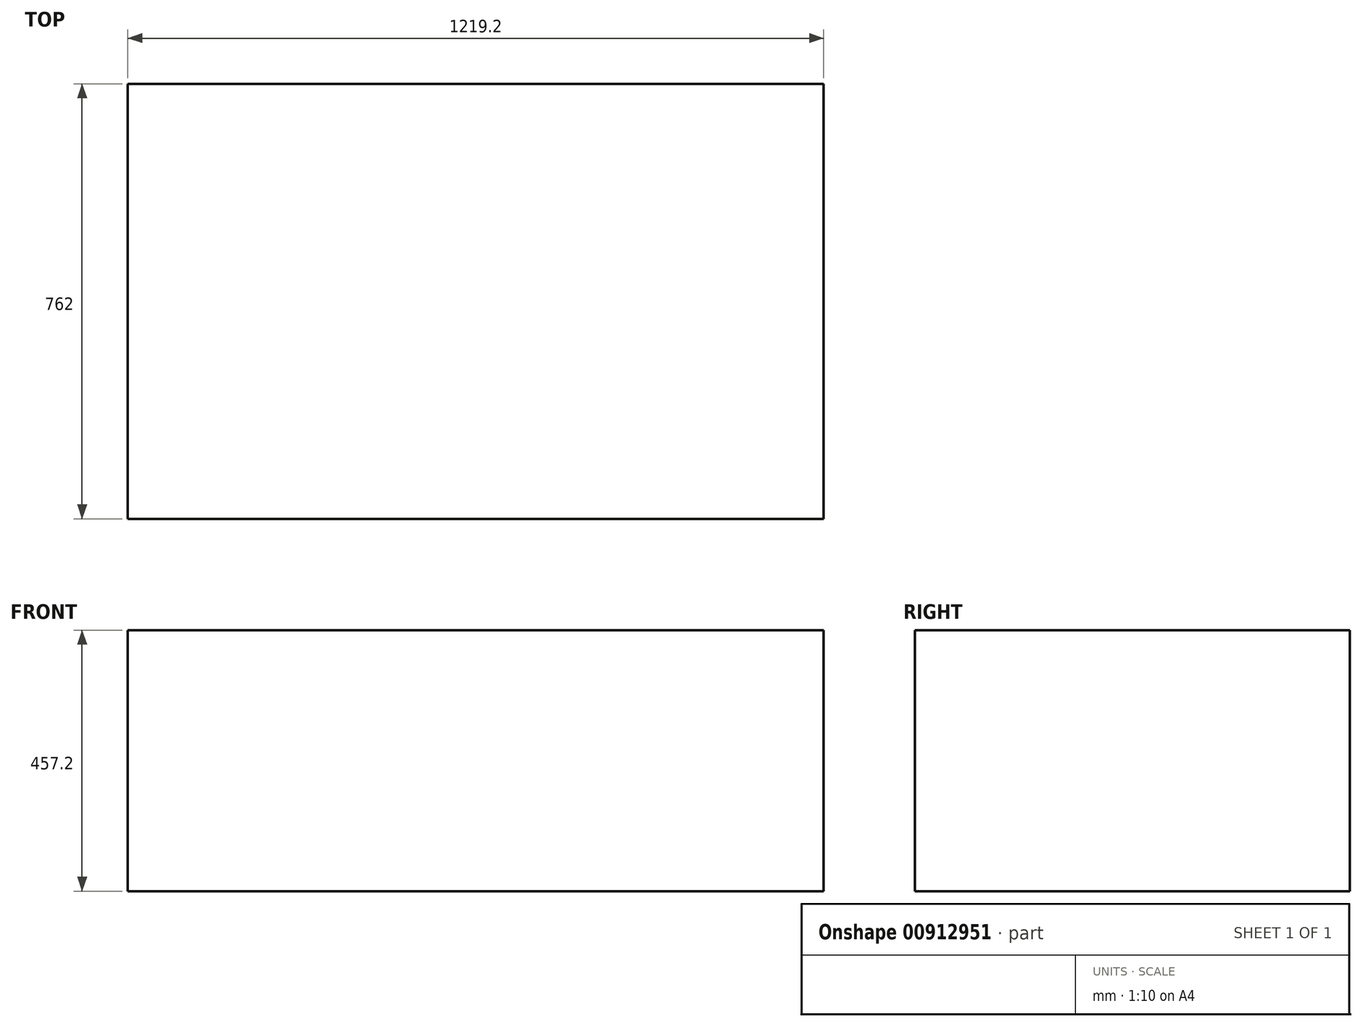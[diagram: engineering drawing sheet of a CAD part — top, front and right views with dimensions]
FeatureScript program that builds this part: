
annotation { "Feature Type Name" : "Feature", "Feature Type Description" : "" }
export const myFeature = defineFeature(function(context is Context, id is Id, definition is map)
    precondition{}
    {
        {
            var Q0;
            Q0=qCreatedBy(makeId("Front.planeOp"),FACE);
            var sketch = newSketch(context, id + "F0", { "sketchPlane" : qUnion([Q0])});
            skLineSegment(sketch, "E0", {"start": v(-609.6, 0) * mm, "end": v(609.6, 0) * mm});
            skLineSegment(sketch, "E1", {"start": v(-609.6, 0) * mm, "end": v(-609.6, 457.2) * mm});
            skLineSegment(sketch, "E2", {"start": v(-609.6, 457.2) * mm, "end": v(609.6, 457.2) * mm});
            skLineSegment(sketch, "E3", {"start": v(609.6, 457.2) * mm, "end": v(609.6, 0) * mm});
            skSolve(sketch);
        }
        {
            var Q0;
            Q0 = qSketchRegion(id + "F0", true);
            extrude(context, id + "F1", {"entities" : qUnion([Q0]), "endBound" : BoundingType.SYMMETRIC, "depth" : 762 * mm, "offsetDistance" : 25.4 * mm});
        }
    });
